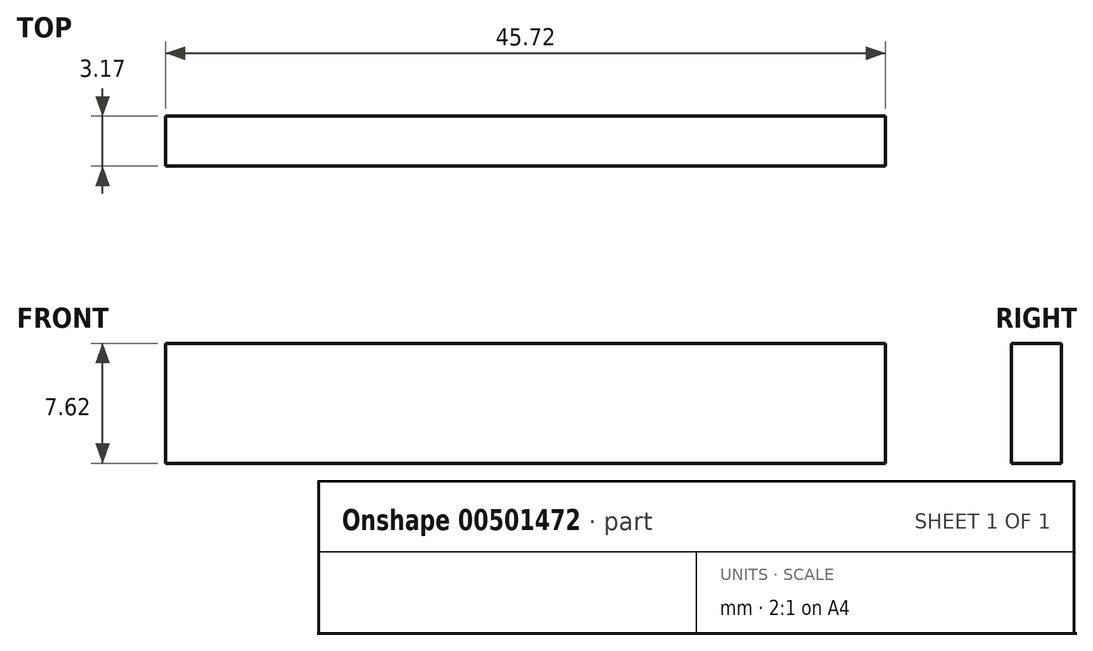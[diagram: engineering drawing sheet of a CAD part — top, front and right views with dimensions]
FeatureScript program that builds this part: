
annotation { "Feature Type Name" : "Feature", "Feature Type Description" : "" }
export const myFeature = defineFeature(function(context is Context, id is Id, definition is map)
    precondition{}
    {
        {
            var Q0;
            Q0=qCreatedBy(makeId("Front.planeOp"),FACE);
            var sketch = newSketch(context, id + "F0", { "sketchPlane" : qUnion([Q0])});
            skLineSegment(sketch, "E0", {"start": v(0, 7.62) * mm, "end": v(0, 0) * mm});
            skLineSegment(sketch, "E1", {"start": v(0, 0) * mm, "end": v(45.72, 0) * mm});
            skLineSegment(sketch, "E2", {"start": v(45.72, 7.62) * mm, "end": v(45.72, 0) * mm});
            skLineSegment(sketch, "E3", {"start": v(0, 7.62) * mm, "end": v(45.72, 7.62) * mm});
            skSolve(sketch);
        }
        {
            var Q0;
            Q0=makeQuery(id+"F0.imprint","IMPRINT",FACE,{"disambiguationData":[TD([[makeQuery(id+"F0.imprint","IMPRINT",EDGE,{"derivedFrom":sQuery(id+"F0.wireOp",EDGE,"E0")}),1.0]])]});
            extrude(context, id + "F1", {"entities" : qUnion([Q0]), "depth" : 3.17 * mm});
        }
        {
            var Q0;
            Q0=makeQuery(id+"F1.opExtrude","CAP_FACE",FACE,{"disambiguationData":[OSD([sQuery(id+"F0.wireOp",EDGE,"E0"),sQuery(id+"F0.wireOp",EDGE,"E1"),sQuery(id+"F0.wireOp",EDGE,"E2"),sQuery(id+"F0.wireOp",EDGE,"E3")])],"isStart":false});
            var sketch = newSketch(context, id + "F2", { "sketchPlane" : qUnion([Q0])});
            skCircle(sketch, "E4", {"center": v(18.12, 4.25) * mm, "radius": 0.86 * mm});
            skCircle(sketch, "E5.1.0.0", {"center": v(28.12, 4.25) * mm, "radius": 0.86 * mm});
            skCircle(sketch, "E5.2.0.0", {"center": v(38.12, 4.25) * mm, "radius": 0.86 * mm});
            skSolve(sketch);
        }
        {
            var Q0;
            Q0=sQuery(id+"F2.wireOp",EDGE,"E4");
            var Q1;
            Q1=sQuery(id+"F2.wireOp",EDGE,"E5.1.0.0");
            var Q2;
            Q2=sQuery(id+"F2.wireOp",EDGE,"E5.2.0.0");
            extrude(context, id + "F3", {"bodyType" : ToolBodyType.SURFACE, "surfaceEntities" : qUnion([Q0, Q1, Q2]), "depth" : 5 * mm});
        }
    });
